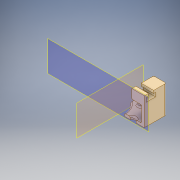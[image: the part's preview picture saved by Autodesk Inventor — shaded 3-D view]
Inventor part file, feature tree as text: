
AUTODESK INVENTOR PART (.ipt)
format: ipt  version: 2017 (Build 210142000, 142)  size: 404,480 bytes
history: native  units: in
note: dims shown in document units (in); Inventor stores cm internally (conversion verified against a paired STEP export)
features: projected_geometry x14, sketch x12, extrude x11, plane x2, hole x1, fillet x1
ambient origin geometry x8: Origin, YZ Plane, XZ Plane, XY Plane, X Axis, Y Axis, Z Axis, Center Point
bodies: Solid1 (feature_tree)
feature tree (41):
  extrude  "Extrusion1"  Depth=3.622in
  extrude  "Extrusion3"  Depth=0.1575in
  extrude  "Extrusion4"  Depth=0.1575in
  extrude  "Extrusion7"  Depth=0.1575in TaperAngle=0.0deg
  extrude  "Extrusion8"  Depth=0.5512in TaperAngle=0.0deg
  extrude  "Extrusion9"  Depth=0.2362in
  hole  "Hole1"  [1 undecoded]
  extrude  "Extrusion10"  Depth=0.3937in
  extrude  "Extrusion11"  Depth=0.748in TaperAngle=0.0deg
  extrude  "Extrusion12"  Depth=0.5512in
  fillet  "Fillet1"  Radius=0.9114in
  plane  "Work Plane1"
  plane  "Work Plane2"
  extrude  "Extrusion13"  Depth=0.3937in
  extrude  "Extrusion14"  Depth=0.0787in TaperAngle=0.0deg
  sketch  "Sketch1"  dims[d0=5.5118in d1=3.622in]
  sketch  "Sketch2"  dims[d2=0.1575in d3=0.0in d4=0.1575in]
  projected_geometry  "Projected Loop1"
  sketch  "Sketch3"  dims[d5=0.1575in d6=0.1575in]
  projected_geometry  "Projected Loop2"
  sketch  "Sketch5"  dims[d7=0.1575in d15=1.5in d16=0.0in]
  projected_geometry  "Projected Loop4"
  sketch  "Sketch6"  dims[d17=0.748in d19=0.5512in d20=0.0in]
  projected_geometry  "Projected Loop5"
  sketch  "Sketch7"  dims[d47=0.5512in d48=0.2362in]
  projected_geometry  "Projected Loop6"
  sketch  "Sketch8"  dims[d49=0.315in d50=0.3937in]
  projected_geometry  "Projected Loop7"
  projected_geometry  "Projected Loop8"
  projected_geometry  "Projected Loop9"
  projected_geometry  "Projected Loop10"
  projected_geometry  "Projected Loop11"
  sketch  "Sketch9"  dims[d51=0.9114in d52=0.5512in d53=0.2362in d54=0.315in d56=0.3937in]
  projected_geometry  "Projected Loop12"
  projected_geometry  "Projected Loop13"
  sketch  "Sketch10"  dims[d57=0.9114in d58=0.748in d59=0.0in]
  projected_geometry  "Projected Loop14"
  sketch  "Sketch11"  dims[d60=0.748in d61=0.5512in d62=0.2362in d63=0.315in]
  projected_geometry  "Projected Loop15"
  sketch  "Sketch12"  dims[d65=0.5512in d66=0.2362in d67=0.315in d68=0.3937in d69=0.3937in d70=0.9114in]
  sketch  "Sketch13"  dims[d71=0.9114in d72=0.3937in d73=0.748in d74=0.0in d75=0.2362in d76=0.2362in d77=1.9291in d78=2.2835in d79=0.2362in d80=0.2362in d82=0.2756in d83=0.2362in d84=0.0in d85=0.1083in d86=0.2362in d87=0.1575in d88=0.0787in d89=90.0deg d90=0.315in d91=0.8108in d92=1.378in d93=0.2362in d94=0.0in d95=0.1875in d96=0.1875in d97=0.1875in d98=0.1875in d99=0.1875in d100=0.1875in d101=0.1875in d102=0.1875in d103=0.0625in d104=0.0in d105=0.315in d106=0.315in d107=0.315in d108=0.315in d109=0.315in d110=0.315in d112=0.315in d113=0.315in d114=0.315in d115=0.315in d116=0.315in d117=0.0625in d118=0.0in d119=-1.3125in d120=-1.5625in d121=0.0787in d122=2.8125in d123=0.0in d124=0.0in d125=0.0in]
note: 1 required parameter value undecoded (feature->parameter linkage not recoverable at this tier; creation-order binding heuristic only, values carry confidence <= 0.55)
